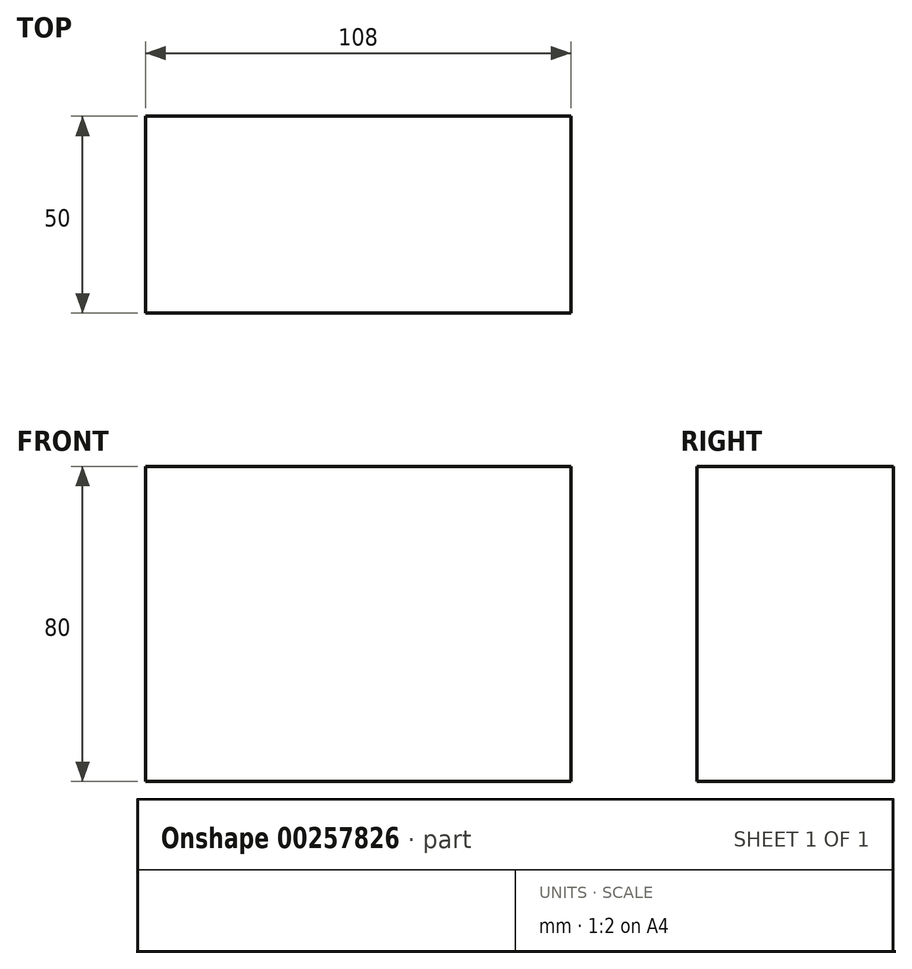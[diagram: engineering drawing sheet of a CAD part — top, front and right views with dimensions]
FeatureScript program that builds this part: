
annotation { "Feature Type Name" : "Feature", "Feature Type Description" : "" }
export const myFeature = defineFeature(function(context is Context, id is Id, definition is map)
    precondition{}
    {
        {
            var Q0;
            Q0=qCreatedBy(makeId("Front.planeOp"),FACE);
            var sketch = newSketch(context, id + "F0", { "sketchPlane" : qUnion([Q0])});
            skLineSegment(sketch, "E0.bottom", {"start": v(-33.56, 43.57) * mm, "end": v(74.44, 43.57) * mm});
            skLineSegment(sketch, "E0.right", {"start": v(74.44, 43.57) * mm, "end": v(74.44, -36.43) * mm});
            skLineSegment(sketch, "E1", {"start": v(-33.56, 43.57) * mm, "end": v(-33.56, -36.43) * mm});
            skLineSegment(sketch, "E2", {"start": v(-33.56, -36.43) * mm, "end": v(74.44, -36.43) * mm});
            skSolve(sketch);
        }
        {
            var Q0;
            Q0=makeQuery(id+"F0.imprint","IMPRINT",FACE,{"disambiguationData":[TD([[makeQuery(id+"F0.imprint","IMPRINT",EDGE,{"derivedFrom":sQuery(id+"F0.wireOp",EDGE,"E0.bottom")}),-1.0]])]});
            var Q1;
            Q1=sQuery(id+"F0.wireOp",EDGE,"E0.bottom");
            extrude(context, id + "F1", {"entities" : qUnion([Q0]), "surfaceEntities" : qUnion([Q1]), "depth" : 50 * mm});
        }
    });
